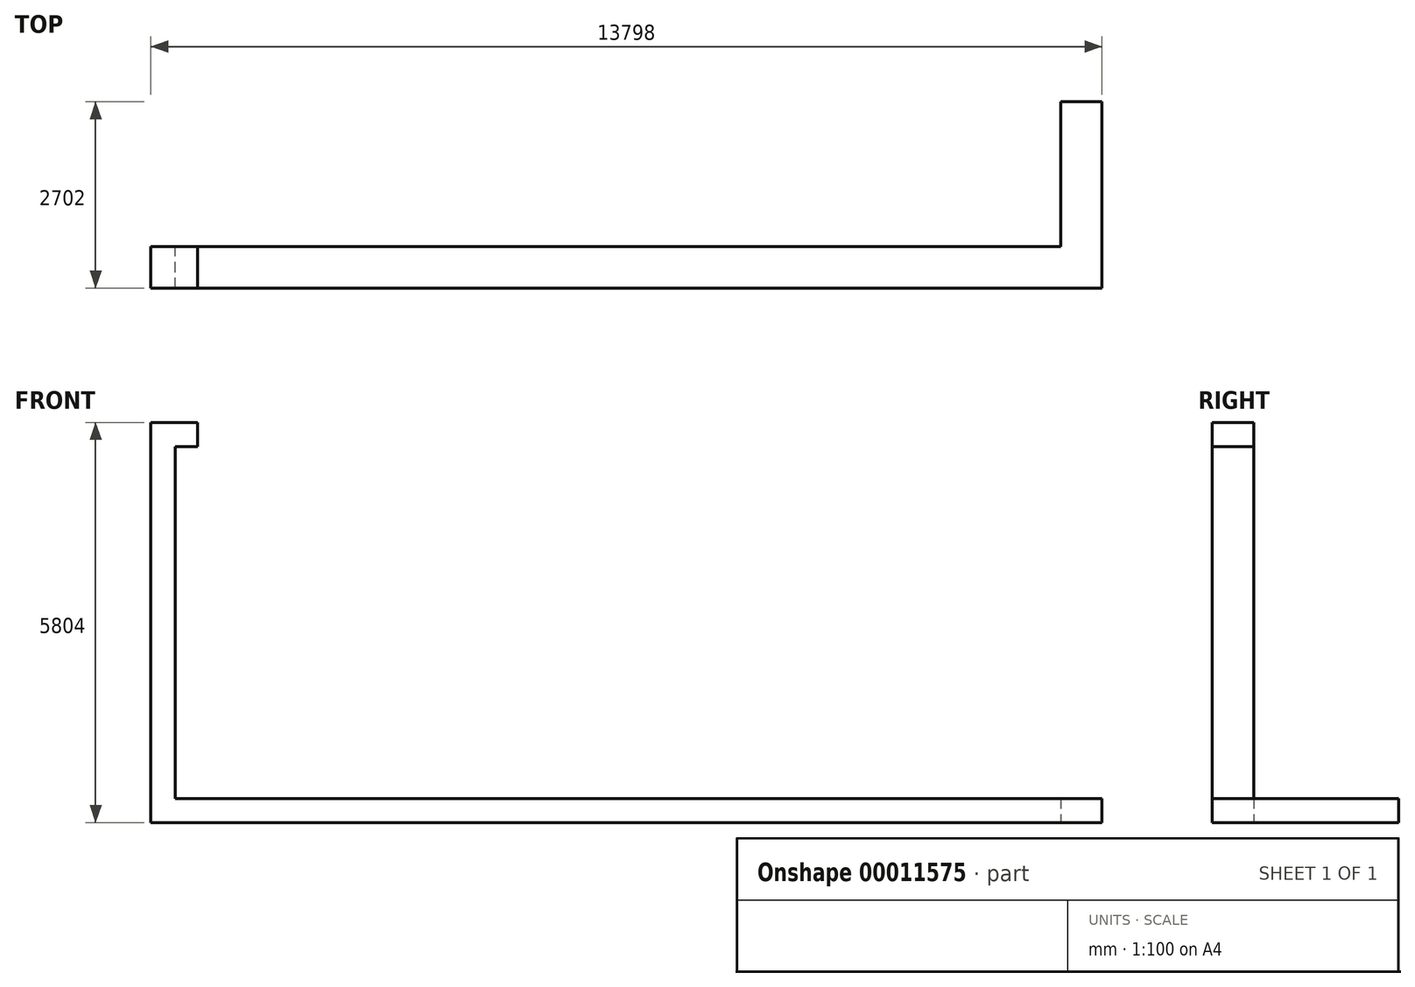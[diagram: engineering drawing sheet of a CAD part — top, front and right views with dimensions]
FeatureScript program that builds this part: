
annotation { "Feature Type Name" : "Feature", "Feature Type Description" : "" }
export const myFeature = defineFeature(function(context is Context, id is Id, definition is map)
    precondition{}
    {
        {
            var Q0;
            Q0=qCreatedBy(makeId("Front.planeOp"),FACE);
            var sketch = newSketch(context, id + "F0", { "sketchPlane" : qUnion([Q0])});
            skLineSegment(sketch, "E0", {"start": v(0, 0) * mm, "end": v(-500, 0) * mm});
            skLineSegment(sketch, "E1", {"start": v(-500, 0) * mm, "end": v(-500, -5454) * mm});
            skLineSegment(sketch, "E2", {"start": v(-500, -5454) * mm, "end": v(12823, -5454) * mm});
            skSolve(sketch);
        }
        {
            var Q0;
            Q0=qCreatedBy(makeId("Right.planeOp"),FACE);
            var sketch = newSketch(context, id + "F1", { "sketchPlane" : qUnion([Q0])});
            skLineSegment(sketch, "E3.rect.bottom", {"start": v(-300, 175) * mm, "end": v(300, 175) * mm});
            skLineSegment(sketch, "E3.rect.top", {"start": v(-300, -175) * mm, "end": v(300, -175) * mm});
            skLineSegment(sketch, "E3.rect.left", {"start": v(-300, 175) * mm, "end": v(-300, -175) * mm});
            skLineSegment(sketch, "E3.rect.right", {"start": v(300, 175) * mm, "end": v(300, -175) * mm});
            skPoint(sketch, "E3.rect.middle", {"position": v(0, 0) * mm});
            skSolve(sketch);
        }
        {
            var Q0;
            Q0=qCreatedBy(makeId("Top.planeOp"),FACE);
            cPlane(context, id + "F2", {"entities" : qUnion([Q0]), "cplaneType" : CPlaneType.OFFSET, "offset" : 5454 * mm, "oppositeDirection" : true, "width" : 150 * mm, "height" : 150 * mm});
        }
        {
            var Q0;
            Q0=qCreatedBy(id+"F2.planeOp",FACE);
            var sketch = newSketch(context, id + "F3", { "sketchPlane" : qUnion([Q0])});
            skLineSegment(sketch, "E4", {"start": v(12823, 0) * mm, "end": v(12823, 2402) * mm});
            skSolve(sketch);
        }
        {
            var Q0;
            Q0=qSketchRegion(id+"F1",true);
            var Q1;
            Q1=qBodyType(qCreatedBy(id+"F0",EDGE),BodyType.WIRE);
            var Q2;
            Q2=sQuery(id+"F3.wireOp",EDGE,"E4");
            sweep(context, id + "F4", {"profiles" : qUnion([Q0]), "path" : qUnion([Q1, Q2])});
        }
    });
